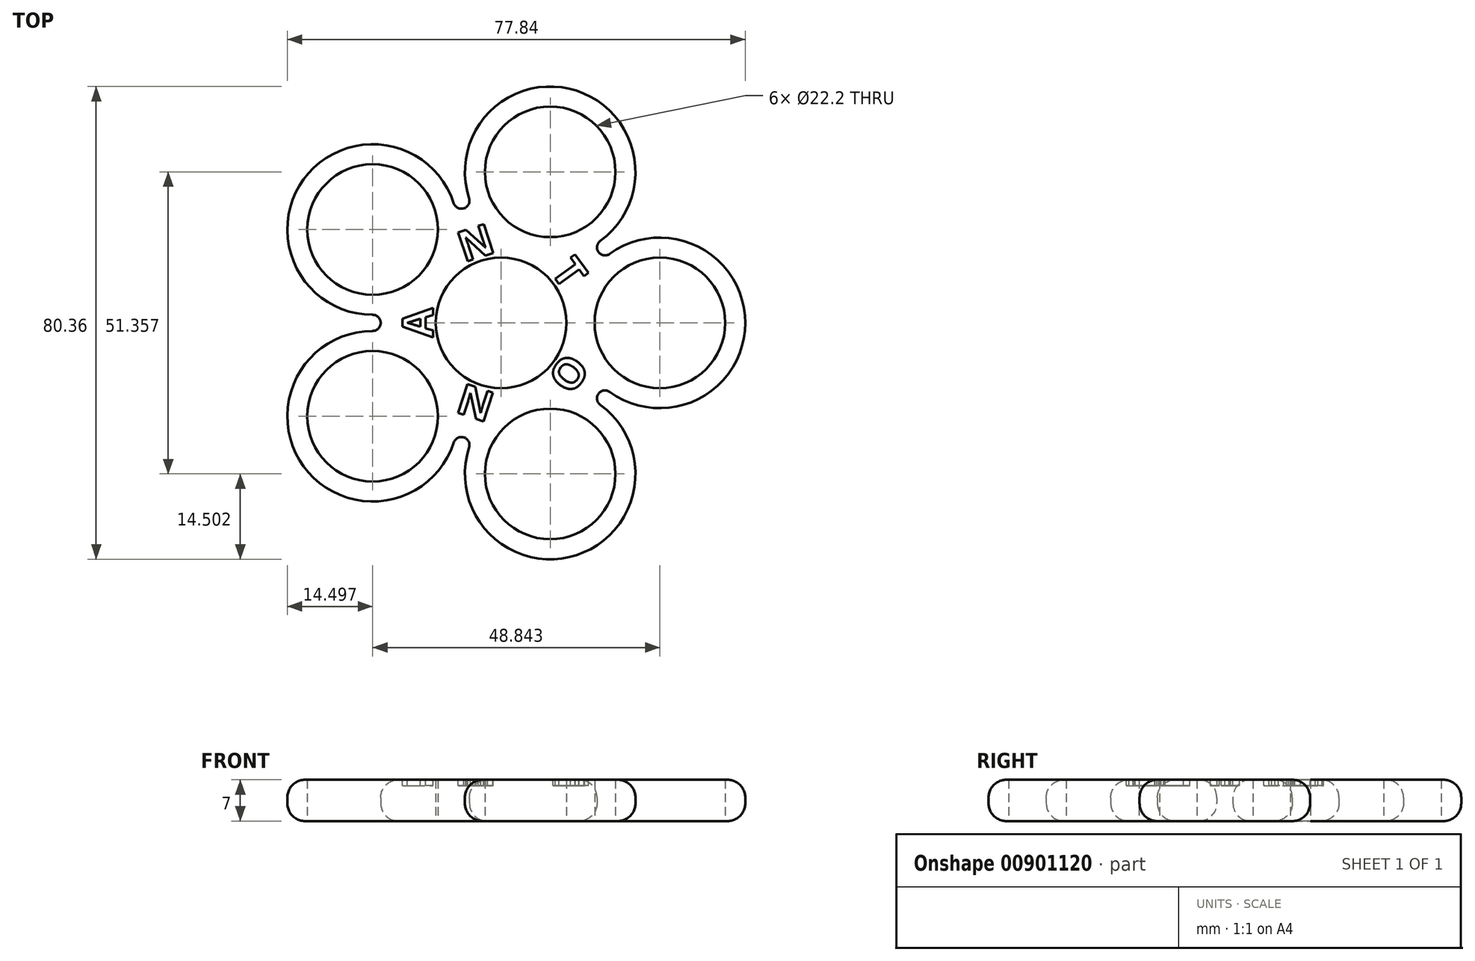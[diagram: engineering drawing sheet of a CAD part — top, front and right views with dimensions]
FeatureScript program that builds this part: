
annotation { "Feature Type Name" : "Feature", "Feature Type Description" : "" }
export const myFeature = defineFeature(function(context is Context, id is Id, definition is map)
    precondition{}
    {
        {
            assignVariable(context, id + "F0", {"name" : "w", "anyValue" : 7});
        }
        {
            var Q0;
            Q0=qCreatedBy(makeId("Top.planeOp"),FACE);
            var sketch = newSketch(context, id + "F1", { "sketchPlane" : qUnion([Q0])});
            skCircle(sketch, "E0", {"center": v(0, 0) * mm, "radius": 11.1 * mm});
            skCircle(sketch, "E1.cCircle", {"center": v(0, 0) * mm, "radius": 27 * mm, "construction": true});
            skLineSegment(sketch, "E1.0", {"start": v(27, 0) * mm, "end": v(8.34, -25.68) * mm, "construction": true});
            skLineSegment(sketch, "E1.1", {"start": v(8.34, -25.68) * mm, "end": v(-21.84, -15.87) * mm, "construction": true});
            skLineSegment(sketch, "E1.2", {"start": v(-21.84, -15.87) * mm, "end": v(-21.84, 15.87) * mm, "construction": true});
            skLineSegment(sketch, "E1.3", {"start": v(-21.84, 15.87) * mm, "end": v(8.34, 25.68) * mm, "construction": true});
            skLineSegment(sketch, "E1.4", {"start": v(8.34, 25.68) * mm, "end": v(27, 0) * mm, "construction": true});
            skCircle(sketch, "E2", {"center": v(27, 0) * mm, "radius": 14.5 * mm});
            skCircle(sketch, "E3", {"center": v(8.34, 25.68) * mm, "radius": 14.5 * mm});
            skCircle(sketch, "E4", {"center": v(-21.84, 15.87) * mm, "radius": 14.5 * mm});
            skCircle(sketch, "E5", {"center": v(-21.84, -15.87) * mm, "radius": 14.5 * mm});
            skCircle(sketch, "E6", {"center": v(8.34, -25.68) * mm, "radius": 14.5 * mm});
            skLineSegment(sketch, "E7", {"start": v(16.87, 13.95) * mm, "end": v(39.22, 30.2) * mm, "construction": true});
            skArc(sketch, "E8", {"start": v(16.87, 13.95) * mm, "mid": v(16.56, 12.03) * mm, "end": v(18.48, 11.73) * mm});
            skLineSegment(sketch, "E9", {"start": v(-8.05, 20.35) * mm, "end": v(-19.48, 55.5) * mm, "construction": true});
            skLineSegment(sketch, "E10", {"start": v(-21.84, -1.37) * mm, "end": v(-57.39, -1.37) * mm, "construction": true});
            skLineSegment(sketch, "E11", {"start": v(-5.45, -21.2) * mm, "end": v(-13.51, -46.02) * mm, "construction": true});
            skLineSegment(sketch, "E12", {"start": v(16.87, -13.95) * mm, "end": v(48.13, -36.66) * mm, "construction": true});
            skArc(sketch, "E13", {"start": v(-8.05, 20.35) * mm, "mid": v(-6.33, 19.47) * mm, "end": v(-5.45, 21.2) * mm});
            skArc(sketch, "E14", {"start": v(-21.84, -1.37) * mm, "mid": v(-20.47, 0) * mm, "end": v(-21.84, 1.37) * mm});
            skArc(sketch, "E15", {"start": v(16.87, -13.95) * mm, "mid": v(16.56, -12.03) * mm, "end": v(18.48, -11.73) * mm});
            skArc(sketch, "E16", {"start": v(-5.45, -21.2) * mm, "mid": v(-6.33, -19.47) * mm, "end": v(-8.05, -20.35) * mm});
            skCircle(sketch, "E17", {"center": v(27, 0) * mm, "radius": 11.1 * mm});
            skCircle(sketch, "E18", {"center": v(8.34, 25.68) * mm, "radius": 11.1 * mm});
            skCircle(sketch, "E19", {"center": v(-21.84, 15.87) * mm, "radius": 11.1 * mm});
            skCircle(sketch, "E20", {"center": v(-21.84, -15.87) * mm, "radius": 11.1 * mm});
            skCircle(sketch, "E21", {"center": v(8.34, -25.68) * mm, "radius": 11.1 * mm});
            skSolve(sketch);
        }
        {
            var Q0;
            Q0=qSketchRegion(id+"F1",true);
            extrude(context, id + "F2", {"entities" : qUnion([Q0]), "endBound" : BoundingType.SYMMETRIC, "depth" : (getVariable(context, 'w')) * mm, "offsetDistance" : 25 * mm});
        }
        {
            var Q0;
            Q0=makeQuery(id+"F2.opExtrude","CAP_EDGE",EDGE,{"disambiguationData":[OSD([sQuery(id+"F1.wireOp",EDGE,"E5")])],"isStart":false});
            var Q1;
            Q1=makeQuery(id+"F2.opExtrude","CAP_EDGE",EDGE,{"disambiguationData":[OSD([sQuery(id+"F1.wireOp",EDGE,"E5")])],"isStart":true});
            fillet(context, id + "F3", {"entities" : qUnion([Q0, Q1]), "radius" : (getVariable(context, 'w') / 2 - 0.5) * mm, "tangentPropagation" : true, "allowEdgeOverflow" : false});
        }
        {
            var Q0;
            Q0=makeQuery(id+"F2.opExtrude","CAP_FACE",FACE,{"disambiguationData":[OSD([sQuery(id+"F1.wireOp",EDGE,"E0"),sQuery(id+"F1.wireOp",EDGE,"E2"),sQuery(id+"F1.wireOp",EDGE,"E3"),sQuery(id+"F1.wireOp",EDGE,"E4"),sQuery(id+"F1.wireOp",EDGE,"E5"),sQuery(id+"F1.wireOp",EDGE,"E6"),sQuery(id+"F1.wireOp",EDGE,"E8"),sQuery(id+"F1.wireOp",EDGE,"E13"),sQuery(id+"F1.wireOp",EDGE,"E14"),sQuery(id+"F1.wireOp",EDGE,"E15"),sQuery(id+"F1.wireOp",EDGE,"E16"),sQuery(id+"F1.wireOp",EDGE,"E17"),sQuery(id+"F1.wireOp",EDGE,"E18"),sQuery(id+"F1.wireOp",EDGE,"E19"),sQuery(id+"F1.wireOp",EDGE,"E20"),sQuery(id+"F1.wireOp",EDGE,"E21")])],"isStart":false});
            var sketch = newSketch(context, id + "F4", { "sketchPlane" : qUnion([Q0])});
            skText(sketch, "E22", { "text": "A", "fontName": "OpenSans-Bold.ttf"});
            skText(sketch, "E23", { "text": "N", "fontName": "OpenSans-Bold.ttf"});
            skText(sketch, "E24", { "text": "T", "fontName": "OpenSans-Bold.ttf"});
            skText(sketch, "E25", { "text": "O", "fontName": "OpenSans-Bold.ttf"});
            skText(sketch, "E26", { "text": "N", "fontName": "OpenSans-Bold.ttf"});
            const initialGuessF4  = {"E22": [-0.01158, -0.00247, 0, 1, 0.0052], "E23": [-0.00631, 0.01028, 0.95106, 0.30902, 0.0052], "E24": [0.0083, 0.00874, 0.58779, -0.80902, 0.0052], "E25": [0.01112, -0.00475, -0.58779, -0.80902, 0.0052], "E26": [-0.00076, -0.01204, -0.95106, 0.30902, 0.0052]};
            skSetInitialGuess(sketch, initialGuessF4);
            skSolve(sketch);
        }
        {
            var Q0;
            Q0 = qSketchRegion(id + "F4", true);
            extrude(context, id + "F5", {"entities" : qUnion([Q0]), "operationType" : NewBodyOperationType.REMOVE, "endBound" : BoundingType.SYMMETRIC, "oppositeDirection" : true, "depth" : 2 * mm, "offsetDistance" : 25 * mm});
        }
    });
